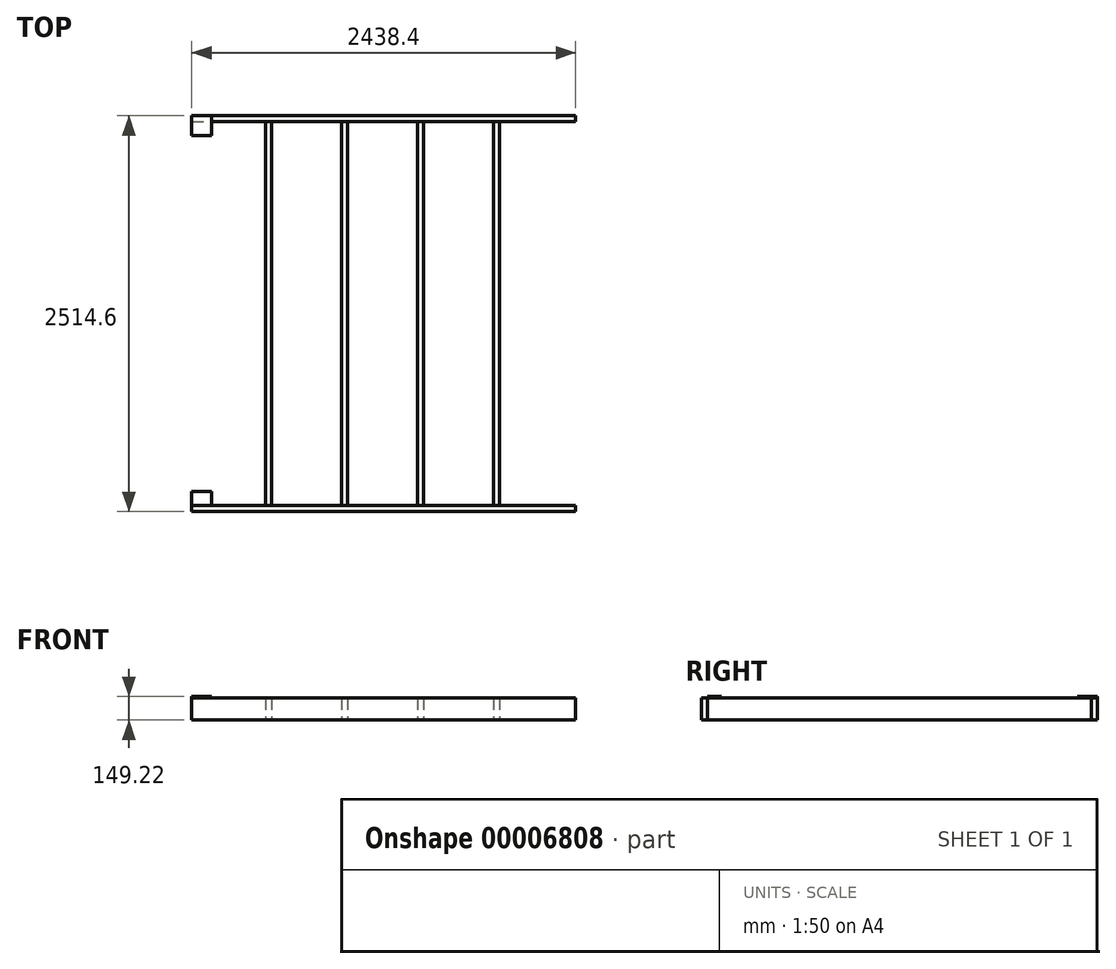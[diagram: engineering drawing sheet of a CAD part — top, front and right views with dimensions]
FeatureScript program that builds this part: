
annotation { "Feature Type Name" : "Feature", "Feature Type Description" : "" }
export const myFeature = defineFeature(function(context is Context, id is Id, definition is map)
    precondition{}
    {
        {
            var Q0;
            Q0=qCreatedBy(makeId("Top.planeOp"),FACE);
            var sketch = newSketch(context, id + "F0", { "sketchPlane" : qUnion([Q0])});
            skLineSegment(sketch, "E0.rect.bottom", {"start": v(1219.2, 1257.3) * mm, "end": v(-1219.2, 1257.3) * mm, "construction": true});
            skLineSegment(sketch, "E0.rect.top", {"start": v(1219.2, -1257.3) * mm, "end": v(-1219.2, -1257.3) * mm, "construction": true});
            skLineSegment(sketch, "E0.rect.left", {"start": v(1219.2, 1257.3) * mm, "end": v(1219.2, -1257.3) * mm, "construction": true});
            skLineSegment(sketch, "E0.rect.right", {"start": v(-1219.2, 1257.3) * mm, "end": v(-1219.2, -1257.3) * mm, "construction": true});
            skPoint(sketch, "E0.rect.middle", {"position": v(0, 0) * mm});
            skLineSegment(sketch, "E1.bottom", {"start": v(-1219.2, -1257.3) * mm, "end": v(1219.2, -1257.3) * mm});
            skLineSegment(sketch, "E1.top", {"start": v(-1219.2, -1219.2) * mm, "end": v(1219.2, -1219.2) * mm});
            skLineSegment(sketch, "E1.left", {"start": v(-1219.2, -1257.3) * mm, "end": v(-1219.2, -1219.2) * mm});
            skLineSegment(sketch, "E1.right", {"start": v(1219.2, -1257.3) * mm, "end": v(1219.2, -1219.2) * mm});
            skLineSegment(sketch, "E2.bottom", {"start": v(-1219.2, 1257.3) * mm, "end": v(1219.2, 1257.3) * mm});
            skLineSegment(sketch, "E2.top", {"start": v(-1219.2, 1219.2) * mm, "end": v(1219.2, 1219.2) * mm});
            skLineSegment(sketch, "E2.left", {"start": v(-1219.2, 1257.3) * mm, "end": v(-1219.2, 1219.2) * mm});
            skLineSegment(sketch, "E2.right", {"start": v(1219.2, 1257.3) * mm, "end": v(1219.2, 1219.2) * mm});
            skLineSegment(sketch, "E3.bottom", {"start": v(-1219.2, 1219.2) * mm, "end": v(-1181.1, 1219.2) * mm});
            skLineSegment(sketch, "E3.top", {"start": v(-1219.2, -1219.2) * mm, "end": v(-1181.1, -1219.2) * mm});
            skLineSegment(sketch, "E3.left", {"start": v(-1219.2, 1219.2) * mm, "end": v(-1219.2, -1219.2) * mm});
            skLineSegment(sketch, "E3.right", {"start": v(-1181.1, 1219.2) * mm, "end": v(-1181.1, -1219.2) * mm});
            skLineSegment(sketch, "E4.bottom", {"start": v(1219.2, 1219.2) * mm, "end": v(1181.1, 1219.2) * mm});
            skLineSegment(sketch, "E4.top", {"start": v(1219.2, -1219.2) * mm, "end": v(1181.1, -1219.2) * mm});
            skLineSegment(sketch, "E4.left", {"start": v(1219.2, 1219.2) * mm, "end": v(1219.2, -1219.2) * mm});
            skLineSegment(sketch, "E4.right", {"start": v(1181.1, 1219.2) * mm, "end": v(1181.1, -1219.2) * mm});
            skLineSegment(sketch, "E5.1.0.0", {"start": v(736.6, 1219.2) * mm, "end": v(736.6, -1219.2) * mm});
            skLineSegment(sketch, "E5.1.0.1", {"start": v(698.5, 1219.2) * mm, "end": v(698.5, -1219.2) * mm});
            skLineSegment(sketch, "E5.2.0.0", {"start": v(254, 1219.2) * mm, "end": v(254, -1219.2) * mm});
            skLineSegment(sketch, "E5.2.0.1", {"start": v(215.9, 1219.2) * mm, "end": v(215.9, -1219.2) * mm});
            skLineSegment(sketch, "E5.3.0.0", {"start": v(-228.6, 1219.2) * mm, "end": v(-228.6, -1219.2) * mm});
            skLineSegment(sketch, "E5.3.0.1", {"start": v(-266.7, 1219.2) * mm, "end": v(-266.7, -1219.2) * mm});
            skLineSegment(sketch, "E5.4.0.0", {"start": v(-711.2, 1219.2) * mm, "end": v(-711.2, -1219.2) * mm});
            skLineSegment(sketch, "E5.4.0.1", {"start": v(-749.3, 1219.2) * mm, "end": v(-749.3, -1219.2) * mm});
            skLineSegment(sketch, "E5.direction1", {"start": v(1219.2, -1219.2) * mm, "end": v(736.6, -1219.2) * mm, "construction": true});
            skSolve(sketch);
        }
        {
            var Q0;
            Q0=makeQuery(id+"F0.imprint","IMPRINT",FACE,{"disambiguationData":[TD([[makeQuery(id+"F0.imprint","IMPRINT",EDGE,{"derivedFrom":sQuery(id+"F0.wireOp",EDGE,"E2.bottom")}),-1.0]])]});
            var Q1;
            Q1=makeQuery(id+"F0.imprint","IMPRINT",FACE,{"disambiguationData":[TD([[makeQuery(id+"F0.imprint","IMPRINT",EDGE,{"derivedFrom":sQuery(id+"F0.wireOp",EDGE,"E1.bottom")}),1.0]])]});
            extrude(context, id + "F1", {"entities" : qUnion([Q0, Q1]), "depth" : 139.7 * mm});
        }
        {
            var Q0;
            Q0=makeQuery(id+"F0.imprint","IMPRINT",FACE,{"disambiguationData":[TD([[makeQuery(id+"F0.imprint","IMPRINT",EDGE,{"derivedFrom":sQuery(id+"F0.wireOp",EDGE,"E3.bottom")}),-1.0]])]});
            var Q1;
            {var subQ1=sQuery(id+"F0.wireOp",EDGE,"E5.4.0.0");Q1=makeQuery(id+"F0.imprint","IMPRINT",FACE,{"disambiguationData":[TD([[makeQuery(id+"F0.imprint","IMPRINT",EDGE,{"derivedFrom":subQ1}),-1.0]])]});}
            var Q2;
            {var subQ1=sQuery(id+"F0.wireOp",EDGE,"E5.3.0.0");Q2=makeQuery(id+"F0.imprint","IMPRINT",FACE,{"disambiguationData":[TD([[makeQuery(id+"F0.imprint","IMPRINT",EDGE,{"derivedFrom":subQ1}),-1.0]])]});}
            var Q3;
            {var subQ1=sQuery(id+"F0.wireOp",EDGE,"E5.2.0.0");Q3=makeQuery(id+"F0.imprint","IMPRINT",FACE,{"disambiguationData":[TD([[makeQuery(id+"F0.imprint","IMPRINT",EDGE,{"derivedFrom":subQ1}),-1.0]])]});}
            var Q4;
            {var subQ1=sQuery(id+"F0.wireOp",EDGE,"E5.1.0.0");Q4=makeQuery(id+"F0.imprint","IMPRINT",FACE,{"disambiguationData":[TD([[makeQuery(id+"F0.imprint","IMPRINT",EDGE,{"derivedFrom":subQ1}),-1.0]])]});}
            var Q5;
            Q5=makeQuery(id+"F0.imprint","IMPRINT",FACE,{"disambiguationData":[TD([[makeQuery(id+"F0.imprint","IMPRINT",EDGE,{"derivedFrom":sQuery(id+"F0.wireOp",EDGE,"E4.bottom")}),1.0]])]});
            extrude(context, id + "F2", {"entities" : qUnion([Q0, Q1, Q2, Q3, Q4, Q5]), "depth" : 139.7 * mm});
        }
        {
            var Q0;
            Q0=makeQuery(id+"F1.opExtrude","CAP_FACE",FACE,{"disambiguationData":[OSD([sQuery(id+"F0.wireOp",EDGE,"E1.bottom"),sQuery(id+"F0.wireOp",EDGE,"E1.top"),sQuery(id+"F0.wireOp",EDGE,"E1.left"),sQuery(id+"F0.wireOp",EDGE,"E1.right"),sQuery(id+"F0.wireOp",EDGE,"E3.top"),sQuery(id+"F0.wireOp",EDGE,"E4.top")])],"isStart":false});
            var sketch = newSketch(context, id + "F3", { "sketchPlane" : qUnion([Q0])});
            skLineSegment(sketch, "E6.0", {"start": v(-1219.2, 1257.3) * mm, "end": v(1219.2, 1257.3) * mm, "construction": true});
            skLineSegment(sketch, "E7.bottom", {"start": v(1219.2, -1257.3) * mm, "end": v(0, -1257.3) * mm});
            skLineSegment(sketch, "E7.top", {"start": v(1219.2, 1257.3) * mm, "end": v(0, 1257.3) * mm});
            skLineSegment(sketch, "E7.left", {"start": v(1219.2, -1257.3) * mm, "end": v(1219.2, 1257.3) * mm});
            skLineSegment(sketch, "E7.right", {"start": v(0, -1257.3) * mm, "end": v(0, 1257.3) * mm});
            skLineSegment(sketch, "E8.bottom", {"start": v(-1219.2, 1257.3) * mm, "end": v(0, 1257.3) * mm});
            skLineSegment(sketch, "E8.top", {"start": v(-1219.2, -1257.3) * mm, "end": v(0, -1257.3) * mm});
            skLineSegment(sketch, "E8.left", {"start": v(-1219.2, 1257.3) * mm, "end": v(-1219.2, -1257.3) * mm});
            skLineSegment(sketch, "E8.right", {"start": v(0, 1257.3) * mm, "end": v(0, -1257.3) * mm});
            skLineSegment(sketch, "E9.0", {"start": v(-1219.2, 1219.2) * mm, "end": v(1219.2, 1219.2) * mm});
            skLineSegment(sketch, "E10.bottom", {"start": v(-1219.2, 1257.3) * mm, "end": v(-1092.2, 1257.3) * mm});
            skLineSegment(sketch, "E10.top", {"start": v(-1219.2, 1130.3) * mm, "end": v(-1092.2, 1130.3) * mm});
            skLineSegment(sketch, "E10.left", {"start": v(-1219.2, 1257.3) * mm, "end": v(-1219.2, 1130.3) * mm});
            skLineSegment(sketch, "E10.right", {"start": v(-1092.2, 1257.3) * mm, "end": v(-1092.2, 1130.3) * mm});
            skLineSegment(sketch, "E11.bottom", {"start": v(-1219.2, -1257.3) * mm, "end": v(-1092.2, -1257.3) * mm});
            skLineSegment(sketch, "E11.top", {"start": v(-1219.2, -1130.3) * mm, "end": v(-1092.2, -1130.3) * mm});
            skLineSegment(sketch, "E11.left", {"start": v(-1219.2, -1257.3) * mm, "end": v(-1219.2, -1130.3) * mm});
            skLineSegment(sketch, "E11.right", {"start": v(-1092.2, -1257.3) * mm, "end": v(-1092.2, -1130.3) * mm});
            skSolve(sketch);
        }
        {
            var Q0;
            Q0=makeQuery(id+"F3.imprint","IMPRINT",FACE,{"disambiguationData":[TD([[makeQuery(id+"F3.imprint","IMPRINT",EDGE,{"derivedFrom":sQuery(id+"F3.wireOp",EDGE,"E8.left")}),1.0]])]});
            extrude(context, id + "F4", {"entities" : qUnion([Q0]), "depth" : 9.52 * mm});
        }
    });
